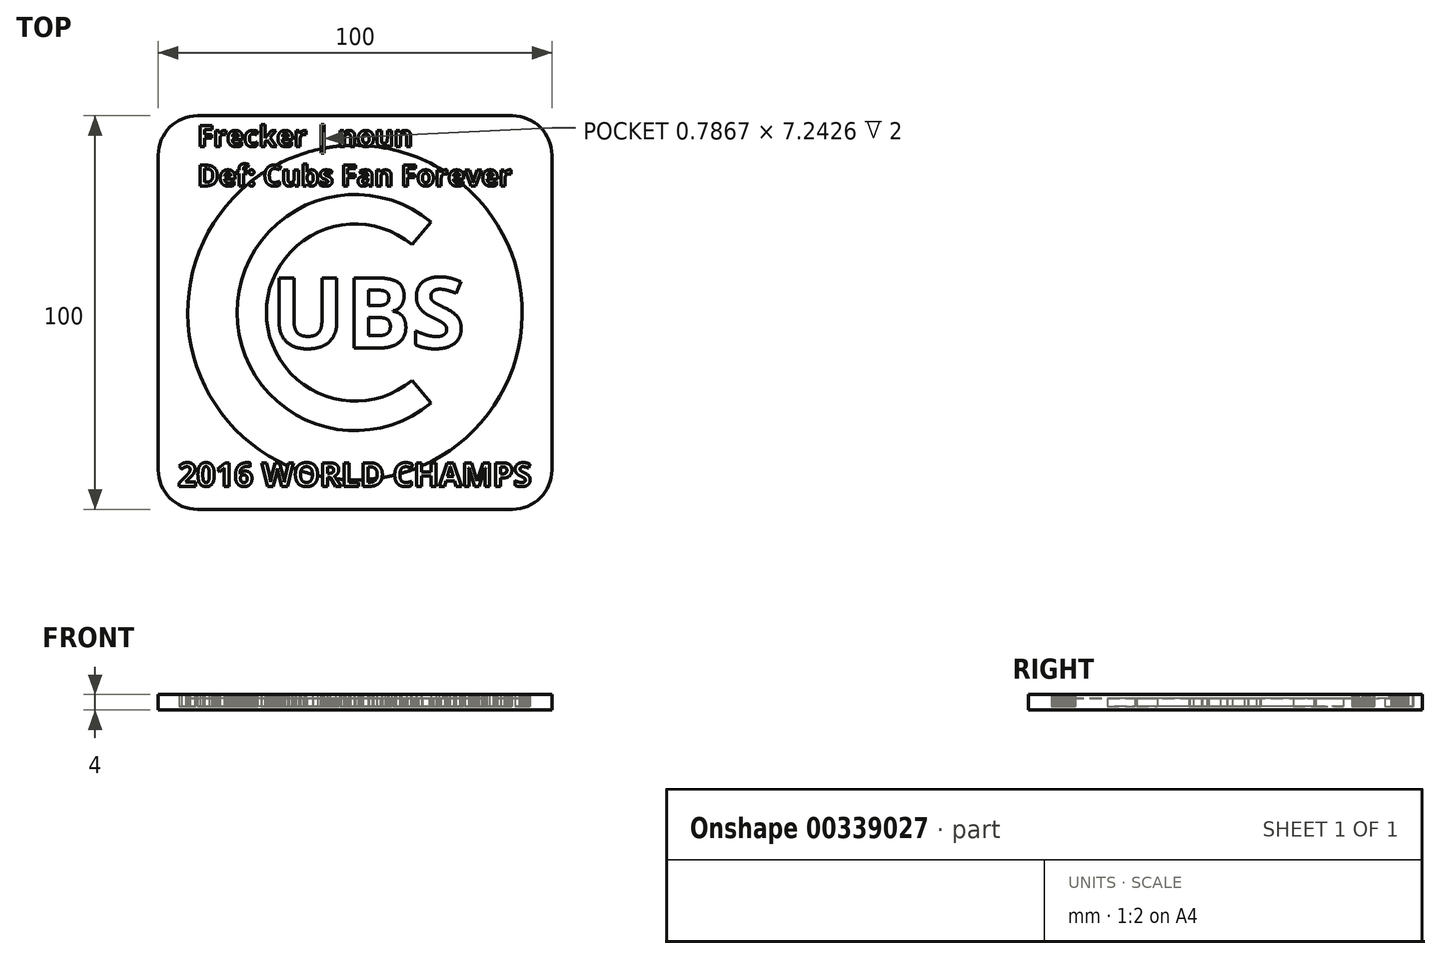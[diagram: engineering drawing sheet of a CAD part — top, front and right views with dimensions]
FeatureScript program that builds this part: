
annotation { "Feature Type Name" : "Feature", "Feature Type Description" : "" }
export const myFeature = defineFeature(function(context is Context, id is Id, definition is map)
    precondition{}
    {
        {
            var Q0;
            Q0=qCreatedBy(makeId("Top.planeOp"),FACE);
            var sketch = newSketch(context, id + "F0", { "sketchPlane" : qUnion([Q0])});
            skLineSegment(sketch, "E0.bottom", {"start": v(-50, 50) * mm, "end": v(50, 50) * mm});
            skLineSegment(sketch, "E0.top", {"start": v(-50, -50) * mm, "end": v(50, -50) * mm});
            skLineSegment(sketch, "E0.left", {"start": v(-50, 50) * mm, "end": v(-50, -50) * mm});
            skLineSegment(sketch, "E0.right", {"start": v(50, 50) * mm, "end": v(50, -50) * mm});
            skSolve(sketch);
        }
        {
            var Q0;
            Q0=makeQuery(id+"F0.imprint","IMPRINT",FACE,{"disambiguationData":[TD([[makeQuery(id+"F0.imprint","IMPRINT",EDGE,{"derivedFrom":sQuery(id+"F0.wireOp",EDGE,"E0.bottom")}),-1.0]])]});
            extrude(context, id + "F1", {"entities" : qUnion([Q0]), "endBound" : BoundingType.SYMMETRIC, "depth" : 4 * mm});
        }
        {
            var Q0;
            Q0=qCreatedBy(makeId("Top.planeOp"),FACE);
            cPlane(context, id + "F2", {"entities" : qUnion([Q0]), "cplaneType" : CPlaneType.OFFSET, "offset" : 1 * mm, "oppositeDirection" : true, "width" : 150 * mm, "height" : 150 * mm});
        }
        {
            var Q0;
            Q0=qCreatedBy(id+"F2.planeOp",FACE);
            var sketch = newSketch(context, id + "F3", { "sketchPlane" : qUnion([Q0])});
            skArc(sketch, "E1", {"start": v(19.28, 22.98) * mm, "mid": v(-30, 0) * mm, "end": v(19.28, -22.98) * mm});
            skArc(sketch, "E2", {"start": v(14.46, 17.24) * mm, "mid": v(-22.5, 0) * mm, "end": v(14.46, -17.24) * mm});
            skText(sketch, "E3", { "text": "UBS", "fontName": "OpenSans-Bold.ttf"});
            skLineSegment(sketch, "E4", {"start": v(14.46, 17.24) * mm, "end": v(19.28, 22.98) * mm});
            skLineSegment(sketch, "E5", {"start": v(14.46, -17.24) * mm, "end": v(19.28, -22.98) * mm});
            skText(sketch, "E6", { "text": "Frecker | noun\nDef: Cubs Fan Forever", "fontName": "OpenSans-Bold.ttf"});
            skText(sketch, "E7", { "text": "2016 WORLD CHAMPS", "fontName": "OpenSans-Bold.ttf"});
            const initialGuessF3  = {"E3": [-0.02138, -0.00898, 1, 0, 0.01796], "E6": [-0.04, 0.0422, 1, 0, 0.0053], "E7": [-0.045, -0.04415, 1, 0, 0.00602]};
            skSetInitialGuess(sketch, initialGuessF3);
            skSolve(sketch);
        }
        {
            var Q0;
            Q0 = qSketchRegion(id + "F3", true);
            extrude(context, id + "F4", {"entities" : qUnion([Q0]), "operationType" : NewBodyOperationType.REMOVE, "oppositeDirection" : true, "depth" : -5 * mm});
        }
        {
            var Q0;
            Q0=makeQuery(id+"F1.opExtrude","CAP_FACE",FACE,{"disambiguationData":[OSD([sQuery(id+"F0.wireOp",EDGE,"E0.bottom"),sQuery(id+"F0.wireOp",EDGE,"E0.top"),sQuery(id+"F0.wireOp",EDGE,"E0.left"),sQuery(id+"F0.wireOp",EDGE,"E0.right")])],"isStart":false});
            var sketch = newSketch(context, id + "F5", { "sketchPlane" : qUnion([Q0])});
            skSolve(sketch);
        }
        {
            var Q0;
            Q0=makeQuery(id+"F5.imprint","IMPRINT",FACE,{"disambiguationData":[TD([[makeQuery(id+"F5.imprint","IMPRINT",EDGE,{"derivedFrom":makeQuery(id+"F1.opExtrude","CAP_EDGE",EDGE,{"disambiguationData":[OSD([sQuery(id+"F0.wireOp",EDGE,"E0.bottom")])],"isStart":false})}),-1.0]])]});
            var sketch = newSketch(context, id + "F6", { "sketchPlane" : qUnion([Q0])});
            skCircle(sketch, "E8", {"center": v(0, 0) * mm, "radius": 42.5 * mm});
            skSolve(sketch);
        }
        {
            var Q0;
            Q0 = qSketchRegion(id + "F6", true);
            extrude(context, id + "F7", {"entities" : qUnion([Q0]), "operationType" : NewBodyOperationType.REMOVE, "oppositeDirection" : true, "depth" : 1 * mm});
        }
        {
            var Q0;
            Q0=makeQuery(id+"F1.opExtrude","SWEPT_EDGE",EDGE,{"disambiguationData":[OSD([sQuery(id+"F0.wireOp",EDGE,"E0.top"),sQuery(id+"F0.wireOp",EDGE,"E0.left")])]});
            var Q1;
            Q1=makeQuery(id+"F1.opExtrude","SWEPT_EDGE",EDGE,{"disambiguationData":[OSD([sQuery(id+"F0.wireOp",EDGE,"E0.bottom"),sQuery(id+"F0.wireOp",EDGE,"E0.left")])]});
            var Q2;
            Q2=makeQuery(id+"F1.opExtrude","SWEPT_EDGE",EDGE,{"disambiguationData":[OSD([sQuery(id+"F0.wireOp",EDGE,"E0.bottom"),sQuery(id+"F0.wireOp",EDGE,"E0.right")])]});
            var Q3;
            Q3=makeQuery(id+"F1.opExtrude","SWEPT_EDGE",EDGE,{"disambiguationData":[OSD([sQuery(id+"F0.wireOp",EDGE,"E0.top"),sQuery(id+"F0.wireOp",EDGE,"E0.right")])]});
            fillet(context, id + "F8", {"entities" : qUnion([Q0, Q1, Q2, Q3]), "radius" : 10 * mm, "tangentPropagation" : true, "allowEdgeOverflow" : false});
        }
    });
